# Revit family: Building-IEC309Connections-GEWISS-IEC309HP-10°_SURFACE-MOUNT_SOCKET_63A_IP67
name_source: partatom
category: Apparecchi elettrici
units: mm (PartAtom-declared; Revit-internal decimal feet)

## family parameters
Condiviso = No
Host = Superficie
Mantenere orientamento annotazione = Sì
Punto di calcolo locali = Sì
Quota connettore circolare = Usa diametro
Taglio con vuoti quando caricato = No
Tipo di parte = Normale

## types (11) — shared parameters
BLOCCO = B=C
Breaking capacity at 1.1 Un = 79A
Catalogue = BUILDING
Corpo centrale = Default(2)
Electrocod = 2211
FORMULA = 1000 mm  [stored 3.28084 ft]
Frequency = 50/60 Hz
Glow wire test: = 850 °C (active parts) - 650 °C (passive parts)
IDF = a99b4e51-d2f9-480d-8e29-7017fde74b5e
IDT = 15153d86c57c49878308f32a8a00a04c
IP degree = IP67
Immagine tipo = <Nessuno>
Insulation resistance = - 10 M?
L = 155 mm
Piastra = Default(2)
Produttore = GEWISS S.p.A.
Prospetto di default = 500 mm
Rated current (A) = 63
SEO = Socket outlet
SPinotto = Default(2)
Shock resistance = IK08
Sportello_visibile = Sì
Spostamento_S = 955 mm
Technical sheet = https://www.gewiss.com
Terminal tightening capacity = 6-16mm² flexible cables - 6-25mm² rigid cables
Thermo-pressure with ball = 125 °C (active parts) - 80 °C (passive parts)
Total number of operations = -2000
Type of wiring = With screw
Typology = 10° angled surface-mounting socket-outlet
URL = https://www.gewiss.com
Version file RFA = 21.11
W = 115 mm  [stored 0.377297 ft]

## per-type parameters (varying)
| type | Colour: | Descrizione | Modello | No. of poles | Operating temperature: | Rated voltage | Reference h |
| GW63449 - IP67 10°W.RECEPTACLE 3P+E 63A 230V 9H | Blue | IP67 10°W.RECEPTACLE 3P+E 63A 230V 9H | GW63449 | 3P+E | -25 +55 °C | 200-250V | 9 |
| GW63451 - IP67 10°W.RECEPTACLE 2P+E 63A 400V 9H | Red | IP67 10°W.RECEPTACLE 2P+E 63A 400V 9H | GW63451 | 2P+E | -25 +55 °C | 380-415V | 9 |
| GW63450 - IP67 10°W.RECEPTACLE 3P+N+T 63A 230V 9H | Blue | IP67 10°W.RECEPTACLE 3P+N+T 63A 230V 9H | GW63450 | 3P+N+E | -25 +55 °C | 200-250V | 9 |
| GW63445 - IP67 10°W.RECEPTACLE 2P+E 63A 110V 4H | Yellow | IP67 10°W.RECEPTACLE 2P+E 63A 110V 4H | GW63445 | 2P+E | -25 +55 °C | 100-130V | 4 |
| GW63452 - IP67 10°W.RECEPTACLE 3P+E 63A 400V 6H | Red | IP67 10°W.RECEPTACLE 3P+E 63A 400V 6H | GW63452 | 3P+E | -25 +55 °C | 380-415V | 6 |
| GW63447 - IP67 10°W.RECEPTACLE 3P+N+T 63A 110V 4H | Yellow | IP67 10°W.RECEPTACLE 3P+N+T 63A 110V 4H | GW63447 | 3P+N+E | -25 +55 °C | 100-130V | 4 |
| GW63453 - IP67 10°W.RECEPTACLE 3P+N+T 63A 400V 6H | Red | IP67 10°W.RECEPTACLE 3P+N+T 63A 400V 6H | GW63453 | 3P+N+E | -25 +40 °C | 380-415V | 6 |
| GW63446 - IP67 10°W.RECEPTACLE 3P+E 63A 110V 4H | Yellow | IP67 10°W.RECEPTACLE 3P+E 63A 110V 4H | GW63446 | 3P+E | -25 +55 °C | 100-130V | 4 |
| GW63455 - IP67 10°W.RECEPTACLE 3P+N+T 63A 500V 7H | Black | IP67 10°W.RECEPTACLE 3P+N+T 63A 500V 7H | GW63455 | 3P+N+E | -25 +55 °C | 480-500V | 7 |
| GW63454 - IP67 10°W.RECEPTACLE 3P+E 63A 500V 7H | Black | IP67 10°W.RECEPTACLE 3P+E 63A 500V 7H | GW63454 | 3P+E | -25 +55 °C | 480-500V | 7 |
| GW63448 - IP67 10°W.RECEPTACLE 2P+E 63A 230V 6H | Blue | IP67 10°W.RECEPTACLE 2P+E 63A 230V 6H | GW63448 | 2P+E | -25 +55 °C | 200-250V | 6 |

note: [stored X ft] marks values corroborated as IEEE doubles in the binary element streams (Revit-internal decimal feet)

## geometry (parser evidence)
native form markers: Sweep x1
no freeform markers — native parametric forms only
